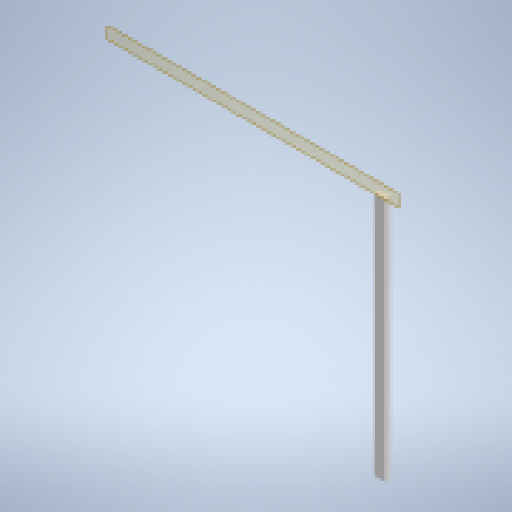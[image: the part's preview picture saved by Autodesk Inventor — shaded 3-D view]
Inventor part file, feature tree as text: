
AUTODESK INVENTOR PART (.ipt)
format: ipt  version: 2025 (Build 290162000, 162)  size: 137,728 bytes
history: native  units: in
note: dims shown in document units (in); Inventor stores cm internally (conversion verified against a paired STEP export)
features: other x3, reference x2, plane x1, extrude x1, sketch x1
ambient origin geometry x8: Origin, YZ Plane, XZ Plane, XY Plane, X Axis, Y Axis, Z Axis, Center Point
bodies: Solid1 (feature_tree)
feature tree (8):
  plane  "Work Plane1"
  extrude  "Extrusion1"  Depth=2.0in TaperAngle=0.0deg
  sketch  "Sketch1"  dims[d0=4.0in d1=2.0in d2=0.0in]
  reference  "Reference1"
  reference  "Reference2"
  other  "Assembly1"
  other  "2x4x96:1"
  other  "2x4x96:2"
